# Revit family: Crealco Skyline Standard Sash Side Hung E
name_source: partatom
category: Windows
revit_build: Autodesk Revit 2014 (Build: 20130308_1515(x64)
units: mm (PartAtom-declared; Revit-internal decimal feet)

## types (18) — shared parameters
Corrected Mullion Configuration = 2 mm  [stored 0.00656168 ft]
Custom Sash Height = 1100 mm  [stored 3.60892 ft]
Custom Sash Width = 500 mm  [stored 1.64042 ft]
Description = Side Hung Type E Standard Sash Window
Frame Profile Thickness = 41 mm  [stored 0.134514 ft]
Heavy Duty Sash = No
Limit Fixed Pane Height Max = 3000 mm  [stored 9.84252 ft]
Limit Fixed Pane Height Min = 200 mm  [stored 0.656168 ft]
Limit Fixed Pane Width Max = 3000 mm  [stored 9.84252 ft]
Limit Fixed Pane Width Min = 200 mm  [stored 0.656168 ft]
Limit Sash Height Max = 1500 mm  [stored 4.92126 ft]
Limit Sash Height Min = 300 mm  [stored 0.984252 ft]
Limit Sash Width Max = 700 mm  [stored 2.29659 ft]
Limit Sash Width Min = 300 mm  [stored 0.984252 ft]
Manufacturer = Crealco
Max System DG Unit Thickness = 25 mm  [stored 0.082021 ft]
Model = Skyline
Rough Width = 3 mm  [stored 0.00984252 ft]
Sash Side Gap = 44 mm
Standard Mullion Different = No
Standard Sash = Yes
URL = www.crealco.co.za
Wall Closure = By host
zero-valued in all types: Custom Frame Offset From Exterior

## per-type parameters (varying)
| type | Clearvue Insulated LowE SHGC Value | Clearvue Insulated LowE U Value | Clearvue Insulated SHGC Value | Clearvue Insulated U Value | Clearvue SHGC Value | Clearvue U Value | Custom Windload | Custom Window Height | Custom Window Width | Energy Advantage SHGC Value | Energy Advantage U Value | Intruderprufe Insulated LowE SHGC Value | Intruderprufe Insulated LowE U Value | Intruderprufe Insulated SHGC Value | Intruderprufe Insulated U Value | Intruderprufe LowE SHGC Value | Intruderprufe LowE U Value | Intruderprufe SHGC Value | Intruderprufe U Value | Toughened Safety SHGC Value | Toughened Safety U Value |
| 0900 x 1500mm 1000Pa | 0.71 | 4.29 | 0.71 | 4.39 | 0.532 | 6.07 | 1000 mm  [stored 3.28084 ft] | 1490 mm  [stored 4.88845 ft] | 890 mm  [stored 2.91995 ft] | 0.479 | 4.93 | 0.59 | 3.22 | 0.59 | 3.29 | 0.446 | 4.77 | 0.501 | 5.88 | 0.532 | 6.07 |
| 0900 x 1500mm 1500Pa | 0.71 | 4.29 | 0.71 | 4.39 | 0.532 | 6.07 | 1500 mm  [stored 4.92126 ft] | 1490 mm  [stored 4.88845 ft] | 890 mm  [stored 2.91995 ft] | 0.479 | 4.93 | 0.59 | 3.22 | 0.59 | 3.29 | 0.446 | 4.77 | 0.501 | 5.88 | 0.532 | 6.07 |
| 0900 x 1500mm 2000Pa | 0.71 | 4.29 | 0.71 | 4.39 | 0.532 | 6.07 | 2000 mm  [stored 6.56168 ft] | 1490 mm  [stored 4.88845 ft] | 890 mm  [stored 2.91995 ft] | 0.479 | 4.93 | 0.59 | 3.22 | 0.59 | 3.29 | 0.446 | 4.77 | 0.501 | 5.88 | 0.532 | 6.07 |
| 1200 x 1500mm 1000Pa | 0.745 | 4.56 | 0.745 | 4.64 | 0.597 | 6.03 | 1000 mm  [stored 3.28084 ft] | 1490 mm  [stored 4.88845 ft] | 1190 mm  [stored 3.9042 ft] | 0.536 | 4.69 | 0.619 | 3.25 | 0.619 | 3.3 | 0.498 | 4.53 | 0.561 | 5.85 | 0.597 | 6.03 |
| 1200 x 1500mm 1500Pa | 0.745 | 4.56 | 0.745 | 4.64 | 0.597 | 6.03 | 1500 mm  [stored 4.92126 ft] | 1490 mm  [stored 4.88845 ft] | 1190 mm  [stored 3.9042 ft] | 0.536 | 4.69 | 0.619 | 3.25 | 0.619 | 3.3 | 0.498 | 4.53 | 0.561 | 5.85 | 0.597 | 6.03 |
| 1200 x 1500mm 2000Pa | 0.746 | 4.7 | 0.746 | 4.78 | 0.586 | 6.1 | 2000 mm  [stored 6.56168 ft] | 1490 mm  [stored 4.88845 ft] | 1190 mm  [stored 3.9042 ft] | 0.526 | 4.8 | 0.62 | 3.38 | 0.62 | 3.43 | 0.489 | 4.64 | 0.551 | 5.91 | 0.586 | 6.1 |
| 1500 x 1500mm 1000Pa | 0.766 | 4.73 | 0.766 | 4.79 | 0.635 | 6.01 | 1000 mm  [stored 3.28084 ft] | 1490 mm  [stored 4.88845 ft] | 1490 mm  [stored 4.88845 ft] | 0.569 | 4.54 | 0.636 | 3.26 | 0.636 | 3.3 | 0.529 | 4.39 | 0.597 | 5.83 | 0.635 | 6.01 |
| 1500 x 1500mm 1500Pa | 0.766 | 4.73 | 0.766 | 4.79 | 0.635 | 6.01 | 1500 mm  [stored 4.92126 ft] | 1490 mm  [stored 4.88845 ft] | 1490 mm  [stored 4.88845 ft] | 0.569 | 4.54 | 0.636 | 3.26 | 0.636 | 3.3 | 0.529 | 4.39 | 0.597 | 5.83 | 0.635 | 6.01 |
| 1500 x 1500mm 2000Pa | 0.767 | 4.84 | 0.767 | 4.9 | 0.626 | 6.06 | 2000 mm  [stored 6.56168 ft] | 1490 mm  [stored 4.88845 ft] | 1490 mm  [stored 4.88845 ft] | 0.562 | 4.63 | 0.637 | 3.37 | 0.637 | 3.41 | 0.522 | 4.48 | 0.589 | 5.87 | 0.626 | 6.06 |
| 0900 x 1800mm 1000Pa | 0.717 | 4.35 | 0.717 | 4.45 | 0.552 | 6.06 | 1000 mm  [stored 3.28084 ft] | 1790 mm  [stored 5.8727 ft] | 890 mm  [stored 2.91995 ft] | 0.497 | 4.86 | 0.596 | 3.23 | 0.596 | 3.3 | 0.462 | 4.69 | 0.52 | 5.86 | 0.552 | 6.06 |
| 0900 x 1800mm 1500Pa | 0.719 | 4.53 | 0.719 | 4.63 | 0.533 | 6.16 | 1500 mm  [stored 4.92126 ft] | 1790 mm  [stored 5.8727 ft] | 890 mm  [stored 2.91995 ft] | 0.48 | 5.03 | 0.598 | 3.41 | 0.598 | 3.48 | 0.446 | 4.85 | 0.502 | 5.94 | 0.533 | 6.16 |
| 0900 x 1800mm 2000Pa | 0.719 | 4.53 | 0.719 | 4.63 | 0.533 | 6.16 | 2000 mm  [stored 6.56168 ft] | 1790 mm  [stored 5.8727 ft] | 890 mm  [stored 2.91995 ft] | 0.48 | 5.03 | 0.598 | 3.41 | 0.598 | 3.48 | 0.446 | 4.85 | 0.502 | 5.94 | 0.533 | 6.16 |
| 1200 x 1800mm 1000Pa | 0.751 | 4.63 | 0.751 | 4.71 | 0.614 | 6.02 | 1000 mm  [stored 3.28084 ft] | 1790 mm  [stored 5.8727 ft] | 1190 mm  [stored 3.9042 ft] | 0.551 | 4.62 | 0.624 | 3.27 | 0.624 | 3.32 | 0.512 | 4.46 | 0.578 | 5.83 | 0.614 | 6.02 |
| 1200 x 1800mm 1500Pa | 0.752 | 4.77 | 0.752 | 4.84 | 0.6 | 6.1 | 1500 mm  [stored 4.92126 ft] | 1790 mm  [stored 5.8727 ft] | 1190 mm  [stored 3.9042 ft] | 0.539 | 4.75 | 0.625 | 3.4 | 0.625 | 3.45 | 0.501 | 4.58 | 0.564 | 5.89 | 0.6 | 6.1 |
| 1200 x 1800mm 2000Pa | 0.752 | 4.77 | 0.752 | 4.84 | 0.6 | 6.1 | 2000 mm  [stored 6.56168 ft] | 1790 mm  [stored 5.8727 ft] | 1190 mm  [stored 3.9042 ft] | 0.539 | 4.75 | 0.625 | 3.4 | 0.625 | 3.45 | 0.501 | 4.58 | 0.564 | 5.89 | 0.6 | 6.1 |
| 1500 x 1800mm 1000Pa | 0.772 | 4.91 | 0.772 | 4.97 | 0.64 | 6.06 | 1000 mm  [stored 3.28084 ft] | 1790 mm  [stored 5.8727 ft] | 1490 mm  [stored 4.88845 ft] | 0.574 | 4.58 | 0.641 | 3.4 | 0.641 | 3.43 | 0.533 | 4.43 | 0.602 | 5.87 | 0.64 | 6.06 |
| 1500 x 1800mm 1500Pa | 0.772 | 4.91 | 0.772 | 4.97 | 0.64 | 6.06 | 1500 mm  [stored 4.92126 ft] | 1790 mm  [stored 5.8727 ft] | 1490 mm  [stored 4.88845 ft] | 0.574 | 4.58 | 0.641 | 3.4 | 0.641 | 3.43 | 0.533 | 4.43 | 0.602 | 5.87 | 0.64 | 6.06 |
| 1500 x 1800mm 2000Pa | 0.772 | 4.91 | 0.772 | 4.97 | 0.64 | 6.06 | 2000 mm  [stored 6.56168 ft] | 1790 mm  [stored 5.8727 ft] | 1490 mm  [stored 4.88845 ft] | 0.574 | 4.58 | 0.641 | 3.4 | 0.641 | 3.43 | 0.533 | 4.43 | 0.602 | 5.87 | 0.64 | 6.06 |

note: [stored X ft] marks values corroborated as IEEE doubles in the binary element streams (Revit-internal decimal feet)

## geometry (parser evidence)
native form markers: Sweep x12
no freeform markers — native parametric forms only
